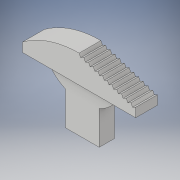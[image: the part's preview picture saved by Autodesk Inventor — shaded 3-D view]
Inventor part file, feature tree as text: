
AUTODESK INVENTOR PART (.ipt)
format: ipt  version: 2018.3 (Build 223284000, 284)  size: 172,032 bytes
history: native  units: in
note: dims shown in document units (in); Inventor stores cm internally (conversion verified against a paired STEP export)
features: extrude x2, sketch x1
ambient origin geometry x8: Origin, YZ Plane, XZ Plane, XY Plane, X Axis, Y Axis, Z Axis, Center Point
bodies: Solid1 (feature_tree)
feature tree (3):
  sketch  "Sketch1"  dims[d3=0.416in d4=0.204in d5=0.7in d6=0.219in d7=0.0183in d9=90.0deg d10=0.0183in d11=90.0deg d12=0.0183in d13=90.0deg d14=0.0183in d15=90.0deg d16=0.0183in d17=90.0deg d18=0.0183in d19=90.0deg d20=0.0183in d21=90.0deg d22=0.0183in d23=90.0deg d24=0.0183in d25=90.0deg d26=0.0183in d27=90.0deg d28=0.0183in d29=90.0deg d32=0.087in d33=0.3in d34=0.55in d35=0.056in d36=0.0in d37=0.08in d38=0.0in]
  extrude  "Extrusion1"  Depth=0.08in
  extrude  "Extrusion2"  Depth=0.08in
